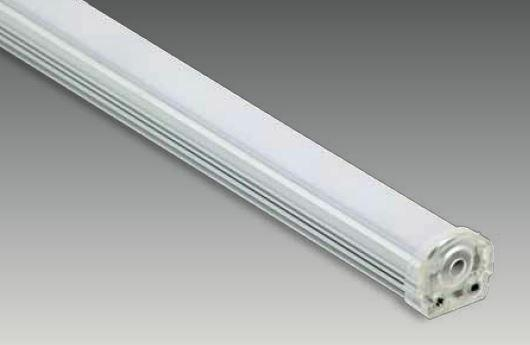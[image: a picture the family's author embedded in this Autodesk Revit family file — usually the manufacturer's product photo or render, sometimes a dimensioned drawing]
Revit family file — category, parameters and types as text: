
# Revit family: SD 0505 CVI
name_source: partatom
category: Lighting Fixtures
revit_build: Autodesk Revit 2017 (Build: 20160225_1515(x64)
units: mm (PartAtom-declared; Revit-internal decimal feet)

## family parameters
Cut with Voids When Loaded = No
Host = Face
Light Source = Yes
Part Type = Normal
Room Calculation Point = No
Round Connector Dimension = Use Diameter
Shared = No

## types (2) — shared parameters
Color Filter = 16777215
Default Elevation = 1219 mm
Dimming Lamp Color Temperature Shift = <None>
Emit Shape Visible in Rendering = Yes
Emit from Rectangle Length = 15 mm  [stored 0.0492126 ft]
Emit from Rectangle Width = 500 mm  [stored 1.64042 ft]
Light Source Symbol Size = 610 mm
Manufacturer = ARLIGHT
Type Image = SD 0505 CVI.JPG
Wattage Comments = 8

## per-type parameters (varying)
| type | Apparent Load |
| SDCVI.505.8.30 | 8 VA |
| SDCVI.505.8.40 | 0 VA |

note: [stored X ft] marks values corroborated as IEEE doubles in the binary element streams (Revit-internal decimal feet)

## geometry (parser evidence)
native form markers: Sweep x3
no freeform markers — native parametric forms only
